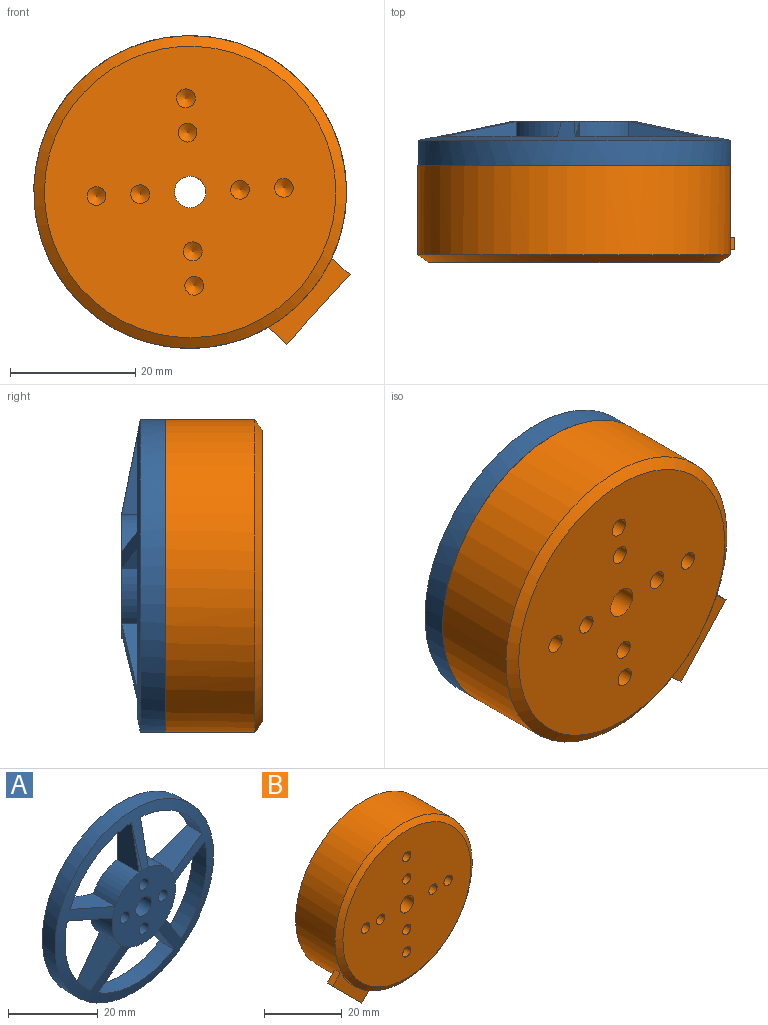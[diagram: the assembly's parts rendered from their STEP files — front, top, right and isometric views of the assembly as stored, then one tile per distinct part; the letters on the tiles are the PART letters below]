
ASSEMBLY  parts=2 mates=1
PART A: 34 faces, bbox 50x7x50 mm
  f0: plane 11.82x7mm, normal (-0.31,0,0.95), area 71.7mm2, adj f1,f15,f23,f24
  f1: cylinder r=10mm len=7.53mm, axis (0,1,0), area 67.8mm2, adj f0,f2,f22,f23
  f2: plane 12.43x7mm, normal (1,0,0), area 71.7mm2, adj f1,f15,f23,f24
  f3: cylinder r=22.37mm len=19.35mm, axis (0,1,0), area 114.2mm2, adj f4,f16,f23,f24
  f4: plane 12.43x7mm, normal (-1,0,0), area 71.7mm2, adj f3,f5,f23,f25
  f5: cylinder r=10mm len=7.53mm, axis (0,1,0), area 67.8mm2, adj f4,f16,f22,f23
  f6: cylinder r=10mm len=8.85mm, axis (0,1,0), area 67.8mm2, adj f7,f17,f22,f23
  f7: plane 10.06x7.31mm, normal (-0.81,0,0.59), area 71.7mm2, adj f6,f8,f23,f24
  f8: cylinder r=22.37mm len=22.75mm, axis (0,1,0), area 114.2mm2, adj f7,f17,f23,f24
  f9: cylinder r=10mm len=9.31mm, axis (0,1,0), area 67.8mm2, adj f10,f18,f22,f23
  f10: plane 10.06x7.31mm, normal (-0.81,0,-0.59), area 71.7mm2, adj f9,f11,f23,f24
  f11: cylinder r=22.37mm len=23.92mm, axis (0,1,0), area 114.2mm2, adj f10,f18,f23,f24
  f12: cylinder r=10mm len=8.85mm, axis (0,1,0), area 67.8mm2, adj f13,f19,f22,f23
  f13: plane 11.82x7mm, normal (0.31,0,-0.95), area 71.7mm2, adj f12,f14,f23,f24
  f14: cylinder r=22.37mm len=22.75mm, axis (0,1,0), area 114.2mm2, adj f13,f19,f23,f24
  f15: cylinder r=22.37mm len=19.35mm, axis (0,1,0), area 114.2mm2, adj f0,f2,f23,f24
  f16: plane 11.82x7mm, normal (0.31,0,0.95), area 71.7mm2, adj f3,f5,f23,f24
  f17: plane 11.82x7mm, normal (-0.31,0,-0.95), area 71.7mm2, adj f6,f8,f23,f24
  f18: plane 10.06x7.31mm, normal (0.81,0,-0.59), area 71.7mm2, adj f9,f11,f23,f24
  f19: plane 10.06x7.31mm, normal (0.81,0,0.59), area 71.7mm2, adj f12,f14,f23,f24
  f20: cylinder r=2.5mm len=7mm, axis (0,1,0), area 110mm2, adj f22,f23
  f21: cylinder r=25mm len=50mm, axis (0,1,0), area 628.3mm2, adj f23,f24
  f22: plane 20x20mm, normal (0,-1,0), area 266.2mm2, adj f1,f5,f6,f9,f12,f20,f24,f25
  f23: plane 50x50mm, normal (0,1,0), area 863.5mm2, adj f0,f1,f2,f3,f4,f5,f6,f7
  f24: cone r=10mm half-angle=78.7deg, axis (0,1,0), area 575.3mm2, adj f0,f2,f3,f7,f8,f10,f11,f13
  f25: cone r=10mm half-angle=78.7deg, axis (0,1,0), area 5mm2, adj f4,f22,f24
  f26: cylinder r=1.5mm len=5mm, axis (0,-1,0), area 47.1mm2, adj f22,f27
  f27: cone r=0mm half-angle=59deg, axis (0,-1,0), area 8.2mm2, adj f26
  f28: cylinder r=1.5mm len=5mm, axis (0,-1,0), area 47.1mm2, adj f22,f29
  f29: cone r=0mm half-angle=59deg, axis (0,-1,0), area 8.2mm2, adj f28
  f30: cylinder r=1.5mm len=5mm, axis (0,-1,0), area 47.1mm2, adj f22,f31
  f31: cone r=0mm half-angle=59deg, axis (0,-1,0), area 8.2mm2, adj f30
  f32: cylinder r=1.5mm len=5mm, axis (0,-1,0), area 47.1mm2, adj f22,f33
  f33: cone r=0mm half-angle=59deg, axis (0,-1,0), area 8.2mm2, adj f32
PART B: 26 faces, bbox 50x15.5x50 mm
  f0: cylinder r=2.5mm len=15.5mm, axis (0,1,0), area 243.5mm2, adj f2,f3
  f1: cylinder r=25mm len=50mm, axis (0,1,0), area 2215.8mm2, adj f3,f4,f21,f22,f24,f25
  f2: plane 46.6x46.6mm, normal (0,-1,0), area 1629.4mm2, adj f0,f4,f5,f7,f9,f11,f13,f15
  f3: plane 50x50mm, normal (0,1,0), area 1943.9mm2, adj f0,f1
  f4: cone r=23.3mm half-angle=54.8deg, axis (0,1,0), area 315.7mm2, adj f1,f2
  f5: cylinder r=1.5mm len=7mm, axis (0,-1,0), area 66mm2, adj f2,f6
  f6: cone r=0mm half-angle=59deg, axis (0,-1,0), area 8.2mm2, adj f5
  f7: cylinder r=1.5mm len=7mm, axis (0,-1,0), area 66mm2, adj f2,f8
  f8: cone r=0mm half-angle=59deg, axis (0,-1,0), area 8.2mm2, adj f7
  f9: cylinder r=1.5mm len=7mm, axis (0,-1,0), area 66mm2, adj f2,f10
  f10: cone r=0mm half-angle=59deg, axis (0,-1,0), area 8.2mm2, adj f9
  f11: cylinder r=1.5mm len=7mm, axis (0,-1,0), area 66mm2, adj f2,f12
  f12: cone r=0mm half-angle=59deg, axis (0,-1,0), area 8.2mm2, adj f11
  f13: cylinder r=1.5mm len=7mm, axis (0,-1,0), area 66mm2, adj f2,f14
  f14: cone r=0mm half-angle=59deg, axis (0,-1,0), area 8.2mm2, adj f13
  f15: cylinder r=1.5mm len=7mm, axis (0,-1,0), area 66mm2, adj f2,f16
  f16: cone r=0mm half-angle=59deg, axis (0,-1,0), area 8.2mm2, adj f15
  f17: cylinder r=1.5mm len=7mm, axis (0,-1,0), area 66mm2, adj f2,f18
  f18: cone r=0mm half-angle=59deg, axis (0,-1,0), area 8.2mm2, adj f17
  f19: cylinder r=1.5mm len=7mm, axis (0,-1,0), area 66mm2, adj f2,f20
  f20: cone r=0mm half-angle=59deg, axis (0,-1,0), area 8.2mm2, adj f19
  f21: plane 2.81x2.81mm, normal (0.71,0,-0.71), area 7.9mm2, adj f1,f23,f24,f25
  f22: plane 2.81x2.81mm, normal (-0.71,0,0.71), area 7.9mm2, adj f1,f23,f24,f25
  f23: plane 10.61x10.61mm, normal (-0.71,0,-0.71), area 30mm2, adj f21,f22,f24,f25
  f24: plane 13.41x13.41mm, normal (0,-1,0), area 47.9mm2, adj f1,f21,f22,f23
  f25: plane 13.41x13.41mm, normal (0,1,0), area 47.9mm2, adj f1,f21,f22,f23
PLACE A rot(axis=(0.03,0,-1),180deg) t=(12.18,7.25,-6.05)mm
PLACE B rot(axis=(0,-1,0),92.5deg) t=(12.18,7.25,-6.05)mm fixed
MATE revolute B.f0 <-> A.f1  axis (0,1,0) through (12.18,7.25,-6.05)mm
